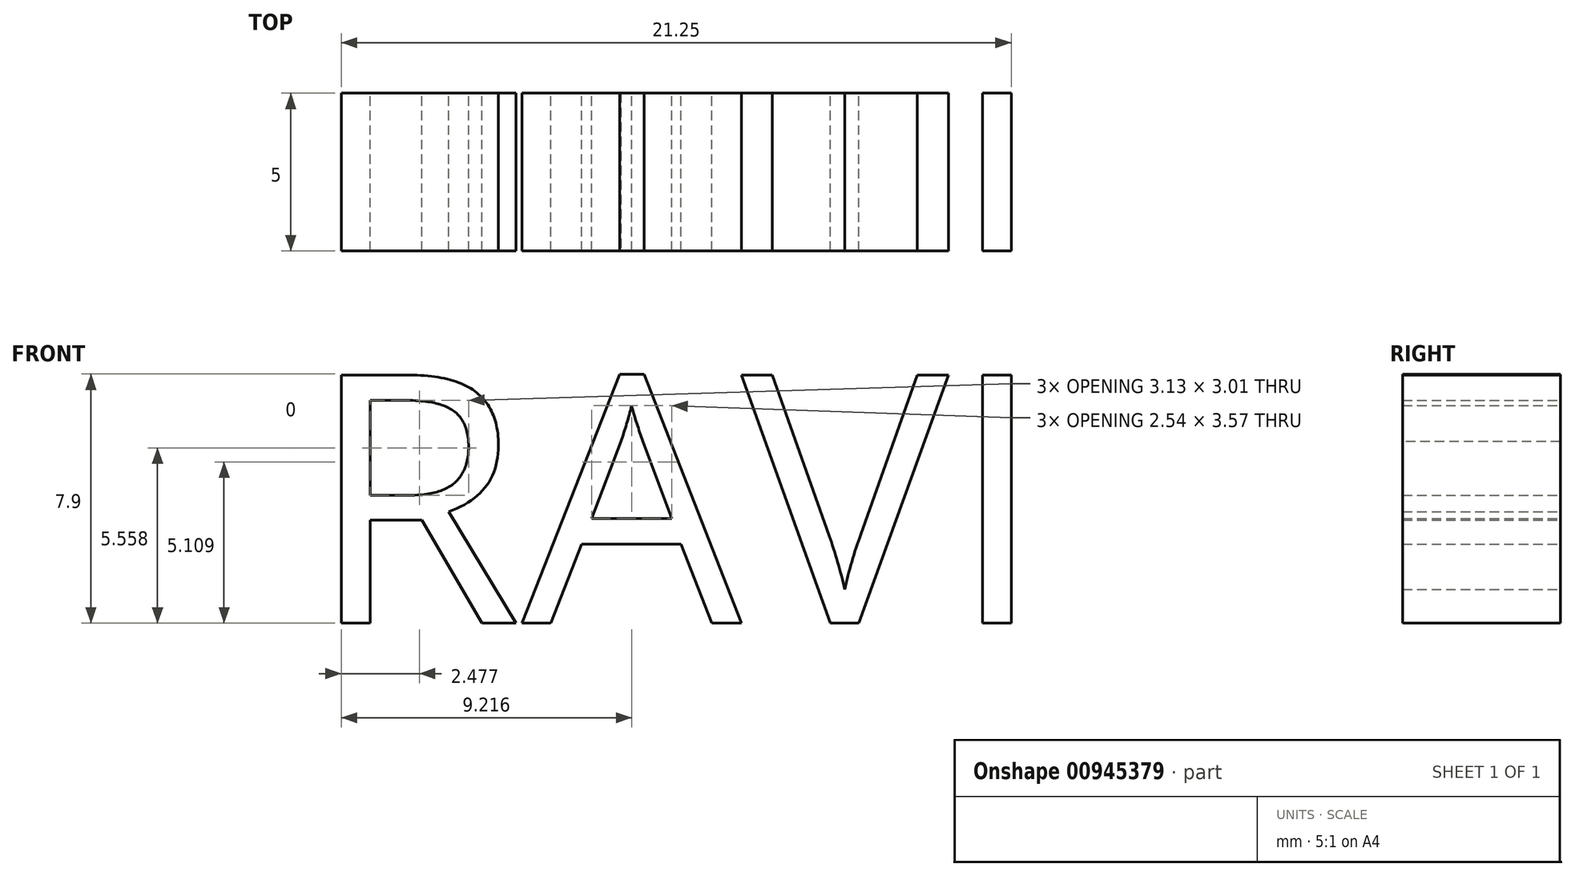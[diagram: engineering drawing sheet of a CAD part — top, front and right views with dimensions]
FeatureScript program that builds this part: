
annotation { "Feature Type Name" : "Feature", "Feature Type Description" : "" }
export const myFeature = defineFeature(function(context is Context, id is Id, definition is map)
    precondition{}
    {
        {
            var Q0;
            Q0=qCreatedBy(makeId("Front.planeOp"),FACE);
            var sketch = newSketch(context, id + "F0", { "sketchPlane" : qUnion([Q0])});
            skText(sketch, "E0", { "text": "RAVI", "fontName": "OpenSans-Regular.ttf"});
            const initialGuessF0  = {"E0": [-0.01204, -0.0041, 1, 0, 0.00793]};
            skSetInitialGuess(sketch, initialGuessF0);
            skSolve(sketch);
        }
        {
            var Q0;
            Q0 = qSketchRegion(id + "F0", true);
            extrude(context, id + "F1", {"entities" : qUnion([Q0]), "depth" : 5 * mm, "offsetDistance" : 25 * mm});
        }
    });
